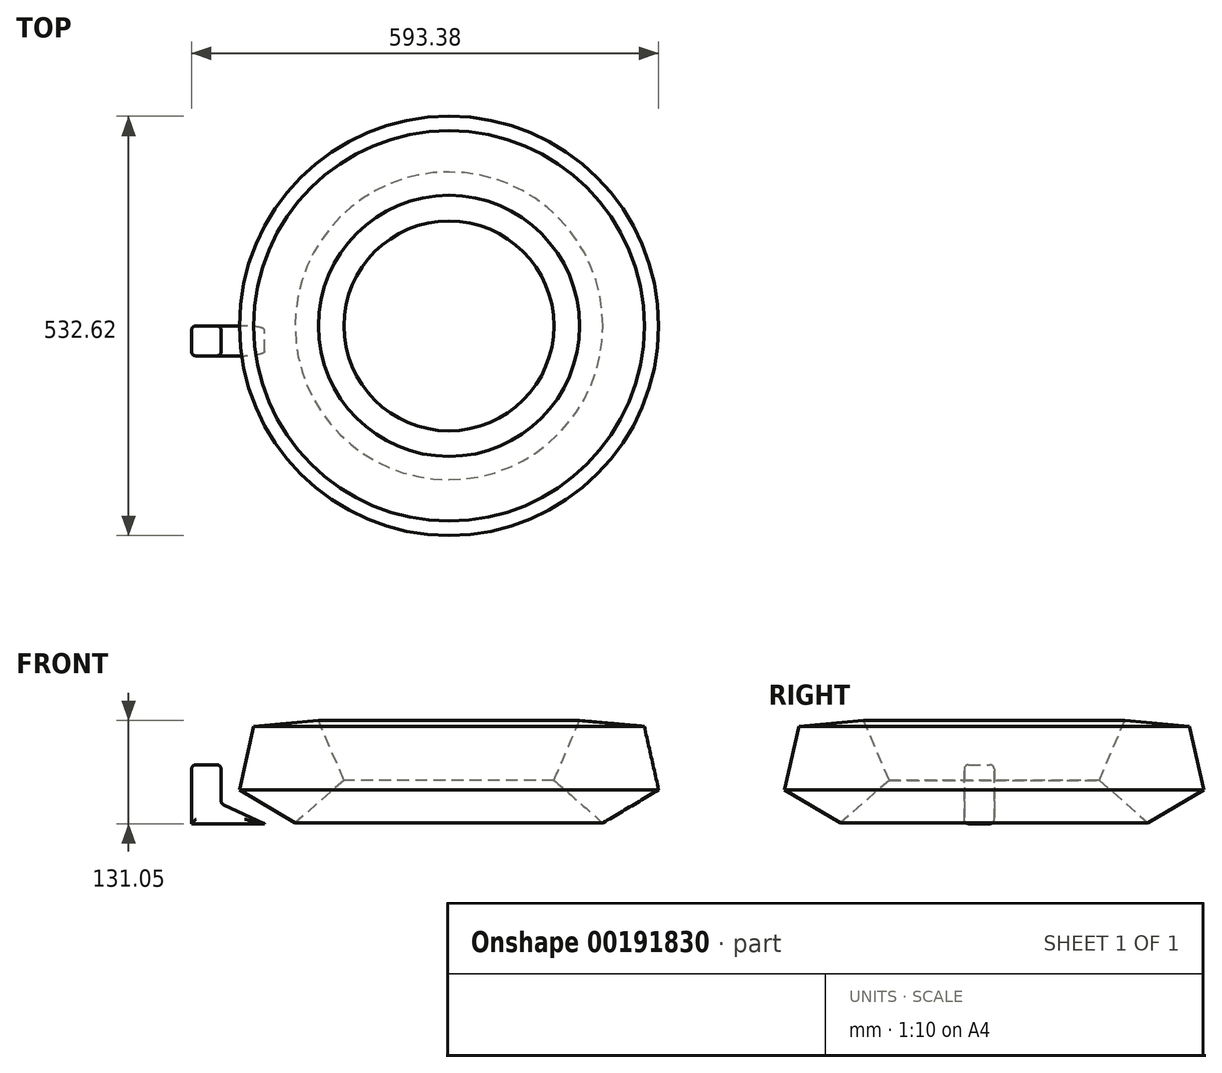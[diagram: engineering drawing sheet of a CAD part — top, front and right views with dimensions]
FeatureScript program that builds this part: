
annotation { "Feature Type Name" : "Feature", "Feature Type Description" : "" }
export const myFeature = defineFeature(function(context is Context, id is Id, definition is map)
    precondition{}
    {
        {
            var Q0;
            Q0=qCreatedBy(makeId("Front.planeOp"),FACE);
            var sketch = newSketch(context, id + "F0", { "sketchPlane" : qUnion([Q0])});
            skLineSegment(sketch, "E0", {"start": v(-37.6, 35.44) * mm, "end": v(-37.6, -36.22) * mm});
            skLineSegment(sketch, "E1", {"start": v(-37.6, -36.22) * mm, "end": v(55.21, -36.22) * mm});
            skLineSegment(sketch, "E2", {"start": v(55.21, -36.22) * mm, "end": v(0, -10.77) * mm});
            skLineSegment(sketch, "E3", {"start": v(0, -10.77) * mm, "end": v(0, 38.57) * mm});
            skLineSegment(sketch, "E4", {"start": v(0, 38.57) * mm, "end": v(-37.6, 38.57) * mm});
            skLineSegment(sketch, "E5", {"start": v(-37.6, 38.57) * mm, "end": v(-37.6, 35.44) * mm});
            skSolve(sketch);
        }
        {
            var Q0;
            Q0=makeQuery(id+"F0.imprint","IMPRINT",FACE,{"disambiguationData":[TD([[makeQuery(id+"F0.imprint","IMPRINT",EDGE,{"derivedFrom":sQuery(id+"F0.wireOp",EDGE,"E0")}),1.0]])]});
            extrude(context, id + "F1", {"entities" : qUnion([Q0]), "depth" : 38.1 * mm});
        }
        {
            var Q0;
            Q0=makeQuery(id+"F1.opExtrude","SWEPT_EDGE",EDGE,{"disambiguationData":[OSD([sQuery(id+"F0.wireOp",EDGE,"E4"),sQuery(id+"F0.wireOp",EDGE,"E5")])]});
            var Q1;
            Q1=makeQuery(id+"F1.opExtrude","SWEPT_EDGE",EDGE,{"disambiguationData":[OSD([sQuery(id+"F0.wireOp",EDGE,"E2"),sQuery(id+"F0.wireOp",EDGE,"E3")])]});
            var Q2;
            Q2=makeQuery(id+"F1.opExtrude","CAP_FACE",FACE,{"disambiguationData":[OSD([sQuery(id+"F0.wireOp",EDGE,"E0"),sQuery(id+"F0.wireOp",EDGE,"E1"),sQuery(id+"F0.wireOp",EDGE,"E2"),sQuery(id+"F0.wireOp",EDGE,"E3"),sQuery(id+"F0.wireOp",EDGE,"E4"),sQuery(id+"F0.wireOp",EDGE,"E5")])],"isStart":false});
            var Q3;
            Q3=makeQuery(id+"F1.opExtrude","CAP_FACE",FACE,{"disambiguationData":[OSD([sQuery(id+"F0.wireOp",EDGE,"E0"),sQuery(id+"F0.wireOp",EDGE,"E1"),sQuery(id+"F0.wireOp",EDGE,"E2"),sQuery(id+"F0.wireOp",EDGE,"E3"),sQuery(id+"F0.wireOp",EDGE,"E4"),sQuery(id+"F0.wireOp",EDGE,"E5")])],"isStart":true});
            var Q4;
            Q4=makeQuery(id+"F1.opExtrude","SWEPT_FACE",FACE,{"disambiguationData":[OSD([sQuery(id+"F0.wireOp",EDGE,"E4")])]});
            var Q5;
            Q5=makeQuery(id+"F1.opExtrude","CAP_EDGE",EDGE,{"disambiguationData":[OSD([sQuery(id+"F0.wireOp",EDGE,"E2")])],"isStart":true});
            fillet(context, id + "F2", {"entities" : qUnion([Q0, Q1, Q2, Q3, Q4, Q5]), "radius" : 5.52 * mm, "tangentPropagation" : true, "allowEdgeOverflow" : false});
        }
        {
            var Q0;
            Q0=qCreatedBy(makeId("Front.planeOp"),FACE);
            var sketch = newSketch(context, id + "F3", { "sketchPlane" : qUnion([Q0])});
            skCircle(sketch, "E6.cCircle", {"center": v(87.68, 34.52) * mm, "radius": 56.8 * mm, "construction": true});
            skLineSegment(sketch, "E6.0", {"start": v(94.06, -35.4) * mm, "end": v(23.16, 6.85) * mm});
            skLineSegment(sketch, "E6.1", {"start": v(23.16, 6.85) * mm, "end": v(41.43, 87.33) * mm});
            skLineSegment(sketch, "E6.2", {"start": v(41.43, 87.33) * mm, "end": v(123.61, 94.83) * mm});
            skLineSegment(sketch, "E6.3", {"start": v(123.61, 94.83) * mm, "end": v(156.15, 18.99) * mm});
            skLineSegment(sketch, "E6.4", {"start": v(156.15, 18.99) * mm, "end": v(94.06, -35.4) * mm});
            skPoint(sketch, "E6.0.midPoint", {"position": v(58.61, -14.27) * mm});
            skLineSegment(sketch, "E7", {"start": v(289.48, 155.54) * mm, "end": v(289.48, -84.4) * mm});
            skSolve(sketch);
        }
        {
            var Q0;
            Q0=makeQuery(id+"F3.imprint","IMPRINT",FACE,{"disambiguationData":[TD([[makeQuery(id+"F3.imprint","IMPRINT",EDGE,{"derivedFrom":sQuery(id+"F3.wireOp",EDGE,"E6.0")}),-1.0]])]});
            var Q1;
            Q1=sQuery(id+"F3.wireOp",EDGE,"E7");
            revolve(context, id + "F4", {"operationType" : NewBodyOperationType.ADD, "entities" : qUnion([Q0]), "axis" : qUnion([Q1]), "revolveType" : RevolveType.FULL});
        }
    });
